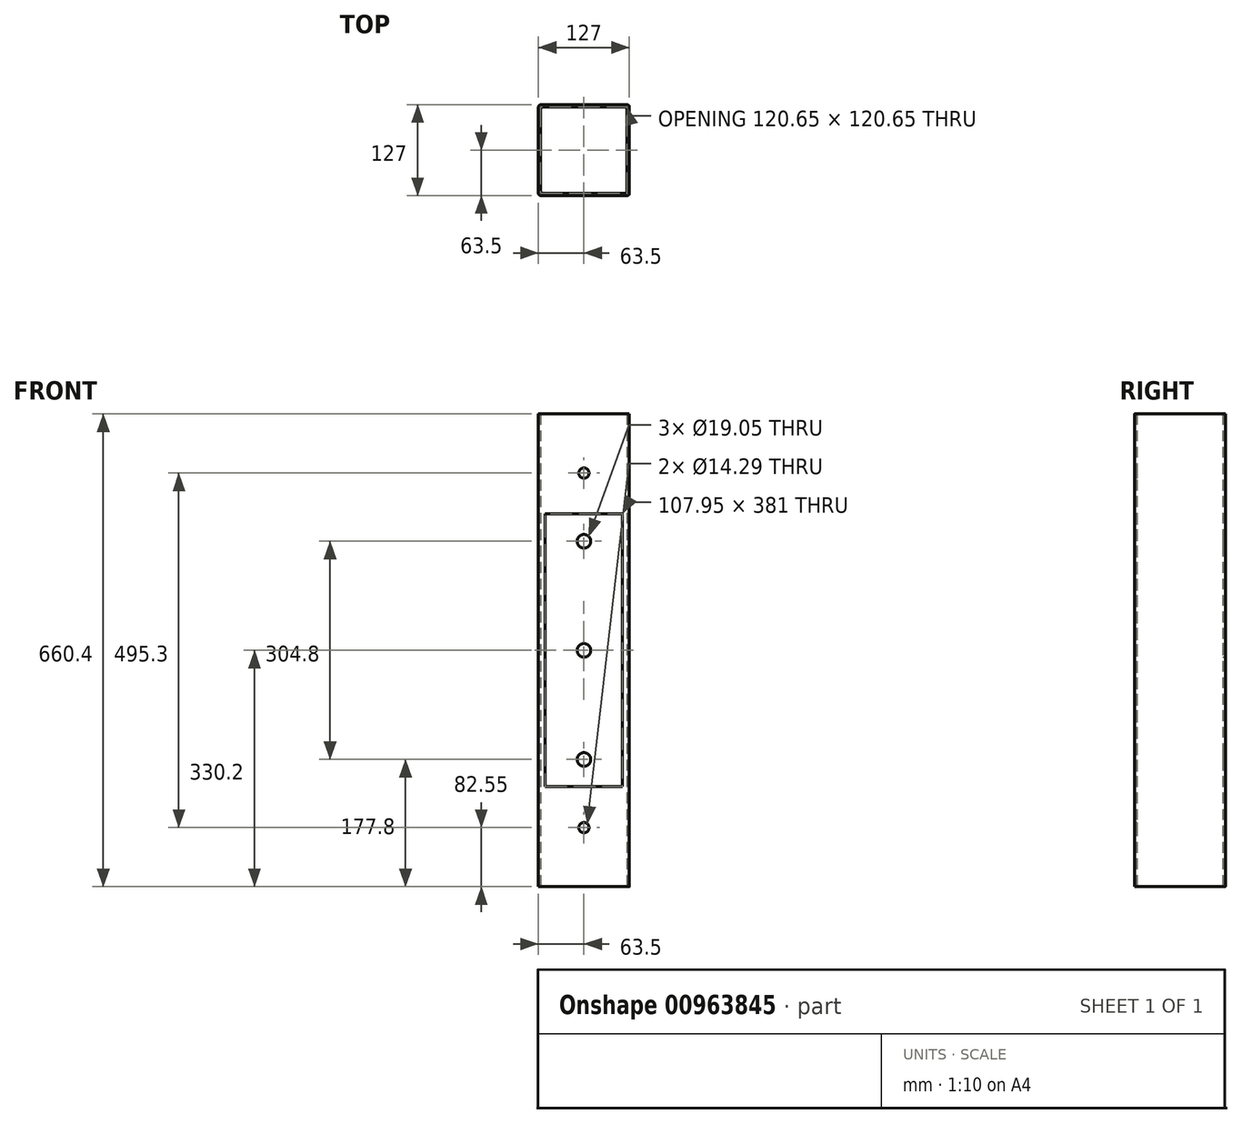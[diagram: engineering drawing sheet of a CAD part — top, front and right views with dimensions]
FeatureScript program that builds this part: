
annotation { "Feature Type Name" : "Feature", "Feature Type Description" : "" }
export const myFeature = defineFeature(function(context is Context, id is Id, definition is map)
    precondition{}
    {
        {
            var Q0;
            Q0=qCreatedBy(makeId("Top.planeOp"),FACE);
            var sketch = newSketch(context, id + "F0", { "sketchPlane" : qUnion([Q0])});
            skLineSegment(sketch, "E0.bottom", {"start": v(-60.33, -60.32) * mm, "end": v(60.32, -60.32) * mm});
            skLineSegment(sketch, "E0.top", {"start": v(-60.33, 60.33) * mm, "end": v(60.33, 60.33) * mm});
            skLineSegment(sketch, "E0.left", {"start": v(-60.33, -60.32) * mm, "end": v(-60.32, 60.33) * mm});
            skLineSegment(sketch, "E0.right", {"start": v(60.33, -60.32) * mm, "end": v(60.33, 60.33) * mm});
            skPoint(sketch, "E0.middle", {"position": v(0, 0) * mm});
            skLineSegment(sketch, "E1.bottom", {"start": v(-63.5, -63.5) * mm, "end": v(63.5, -63.5) * mm});
            skLineSegment(sketch, "E1.top", {"start": v(-63.5, 63.5) * mm, "end": v(63.5, 63.5) * mm});
            skLineSegment(sketch, "E1.left", {"start": v(-63.5, -63.5) * mm, "end": v(-63.5, 63.5) * mm});
            skLineSegment(sketch, "E1.right", {"start": v(63.5, -63.5) * mm, "end": v(63.5, 63.5) * mm});
            skSolve(sketch);
        }
        {
            var Q0;
            Q0=makeQuery(id+"F0.imprint","IMPRINT",FACE,{"disambiguationData":[TD([[makeQuery(id+"F0.imprint","IMPRINT",EDGE,{"derivedFrom":sQuery(id+"F0.wireOp",EDGE,"E0.bottom")}),-1.0]])]});
            extrude(context, id + "F1", {"entities" : qUnion([Q0]), "depth" : 660.4 * mm, "offsetDistance" : 25.4 * mm});
        }
        {
            var Q0;
            Q0=makeQuery(id+"F1.opExtrude","SWEPT_EDGE",EDGE,{"disambiguationData":[OSD([sQuery(id+"F0.wireOp",EDGE,"E0.top"),sQuery(id+"F0.wireOp",EDGE,"E0.right")])]});
            var Q1;
            Q1=makeQuery(id+"F1.opExtrude","SWEPT_EDGE",EDGE,{"disambiguationData":[OSD([sQuery(id+"F0.wireOp",EDGE,"E1.bottom"),sQuery(id+"F0.wireOp",EDGE,"E1.right")])]});
            var Q2;
            Q2=makeQuery(id+"F1.opExtrude","SWEPT_EDGE",EDGE,{"disambiguationData":[OSD([sQuery(id+"F0.wireOp",EDGE,"E1.bottom"),sQuery(id+"F0.wireOp",EDGE,"E1.left")])]});
            var Q3;
            Q3=makeQuery(id+"F1.opExtrude","SWEPT_EDGE",EDGE,{"disambiguationData":[OSD([sQuery(id+"F0.wireOp",EDGE,"E1.top"),sQuery(id+"F0.wireOp",EDGE,"E1.left")])]});
            var Q4;
            Q4=makeQuery(id+"F1.opExtrude","SWEPT_EDGE",EDGE,{"disambiguationData":[OSD([sQuery(id+"F0.wireOp",EDGE,"E0.bottom"),sQuery(id+"F0.wireOp",EDGE,"E0.right")])]});
            var Q5;
            Q5=makeQuery(id+"F1.opExtrude","SWEPT_EDGE",EDGE,{"disambiguationData":[OSD([sQuery(id+"F0.wireOp",EDGE,"E1.top"),sQuery(id+"F0.wireOp",EDGE,"E1.right")])]});
            var Q6;
            Q6=makeQuery(id+"F1.opExtrude","SWEPT_EDGE",EDGE,{"disambiguationData":[OSD([sQuery(id+"F0.wireOp",EDGE,"E0.bottom"),sQuery(id+"F0.wireOp",EDGE,"E0.left")])]});
            fillet(context, id + "F2", {"entities" : qUnion([Q0, Q1, Q2, Q3, Q4, Q5, Q6]), "radius" : 3.17 * mm, "tangentPropagation" : true, "allowEdgeOverflow" : false});
        }
        {
            var Q0;
            Q0=makeQuery(id+"F1.opExtrude","SWEPT_EDGE",EDGE,{"disambiguationData":[OSD([sQuery(id+"F0.wireOp",EDGE,"E0.top"),sQuery(id+"F0.wireOp",EDGE,"E0.left")])]});
            fillet(context, id + "F3", {"entities" : qUnion([Q0]), "radius" : 3.17 * mm, "tangentPropagation" : true, "allowEdgeOverflow" : false});
        }
        {
            var Q0;
            Q0=makeQuery(id+"F1.opExtrude","SWEPT_FACE",FACE,{"disambiguationData":[OSD([sQuery(id+"F0.wireOp",EDGE,"E1.bottom")])]});
            var sketch = newSketch(context, id + "F4", { "sketchPlane" : qUnion([Q0])});
            skLineSegment(sketch, "E2.bottom", {"start": v(53.98, 139.7) * mm, "end": v(-53.98, 139.7) * mm});
            skLineSegment(sketch, "E2.top", {"start": v(53.98, 520.7) * mm, "end": v(-53.97, 520.7) * mm});
            skLineSegment(sketch, "E2.left", {"start": v(53.97, 139.7) * mm, "end": v(53.98, 520.7) * mm});
            skLineSegment(sketch, "E2.right", {"start": v(-53.98, 139.7) * mm, "end": v(-53.97, 520.7) * mm});
            skPoint(sketch, "E2.middle", {"position": v(0, 330.2) * mm});
            skPoint(sketch, "E2.middle.positionSnap0", {"position": v(60.33, 330.2) * mm});
            skPoint(sketch, "E2.centerSnap0", {"position": v(60.33, 330.2) * mm});
            skSolve(sketch);
        }
        {
            var Q0;
            Q0=makeQuery(id+"F4.imprint","IMPRINT",FACE,{"disambiguationData":[TD([[makeQuery(id+"F4.imprint","IMPRINT",EDGE,{"derivedFrom":sQuery(id+"F4.wireOp",EDGE,"E2.bottom")}),-1.0]])]});
            extrude(context, id + "F5", {"entities" : qUnion([Q0]), "operationType" : NewBodyOperationType.REMOVE, "oppositeDirection" : true, "depth" : 25.4 * mm, "offsetDistance" : 25.4 * mm});
        }
        {
            var Q0;
            Q0=makeQuery(id+"F1.opExtrude","SWEPT_FACE",FACE,{"disambiguationData":[OSD([sQuery(id+"F0.wireOp",EDGE,"E1.bottom")])]});
            var sketch = newSketch(context, id + "F6", { "sketchPlane" : qUnion([Q0])});
            skLineSegment(sketch, "E3", {"start": v(0, 660.4) * mm, "end": v(0, 520.7) * mm, "construction": true});
            skLineSegment(sketch, "E4", {"start": v(0, 520.7) * mm, "end": v(0, 577.85) * mm, "construction": true});
            skLineSegment(sketch, "E5", {"start": v(0, 139.7) * mm, "end": v(0, 82.55) * mm, "construction": true});
            skCircle(sketch, "E6", {"center": v(0, 82.55) * mm, "radius": 7.14 * mm});
            skCircle(sketch, "E7", {"center": v(0, 577.85) * mm, "radius": 7.14 * mm});
            skSolve(sketch);
        }
        {
            var Q0;
            Q0 = qSketchRegion(id + "F6", true);
            extrude(context, id + "F7", {"entities" : qUnion([Q0]), "operationType" : NewBodyOperationType.REMOVE, "oppositeDirection" : true, "depth" : 25.4 * mm, "offsetDistance" : 25.4 * mm});
        }
        {
            var Q0;
            Q0=makeQuery(id+"F1.opExtrude","SWEPT_FACE",FACE,{"disambiguationData":[OSD([sQuery(id+"F0.wireOp",EDGE,"E1.top")])]});
            var sketch = newSketch(context, id + "F8", { "sketchPlane" : qUnion([Q0])});
            skLineSegment(sketch, "E8", {"start": v(0, 660.4) * mm, "end": v(0, 482.6) * mm, "construction": true});
            skLineSegment(sketch, "E9", {"start": v(0, 482.6) * mm, "end": v(0, 330.2) * mm, "construction": true});
            skLineSegment(sketch, "E10", {"start": v(0, 0) * mm, "end": v(0, 177.8) * mm, "construction": true});
            skCircle(sketch, "E11", {"center": v(0, 482.6) * mm, "radius": 9.53 * mm});
            skCircle(sketch, "E12", {"center": v(0, 177.8) * mm, "radius": 9.52 * mm});
            skCircle(sketch, "E13", {"center": v(0, 330.2) * mm, "radius": 9.53 * mm});
            skSolve(sketch);
        }
        {
            var Q0;
            Q0=makeQuery(id+"F8.imprint","IMPRINT",FACE,{"disambiguationData":[TD([[makeQuery(id+"F8.imprint","IMPRINT",EDGE,{"derivedFrom":sQuery(id+"F8.wireOp",EDGE,"E12")}),1.0]])]});
            var Q1;
            Q1=makeQuery(id+"F8.imprint","IMPRINT",FACE,{"disambiguationData":[TD([[makeQuery(id+"F8.imprint","IMPRINT",EDGE,{"derivedFrom":sQuery(id+"F8.wireOp",EDGE,"E13")}),1.0]])]});
            var Q2;
            Q2=makeQuery(id+"F8.imprint","IMPRINT",FACE,{"disambiguationData":[TD([[makeQuery(id+"F8.imprint","IMPRINT",EDGE,{"derivedFrom":sQuery(id+"F8.wireOp",EDGE,"E11")}),1.0]])]});
            extrude(context, id + "F9", {"entities" : qUnion([Q0, Q1, Q2]), "operationType" : NewBodyOperationType.REMOVE, "oppositeDirection" : true, "depth" : 25.4 * mm, "offsetDistance" : 25.4 * mm});
        }
    });
